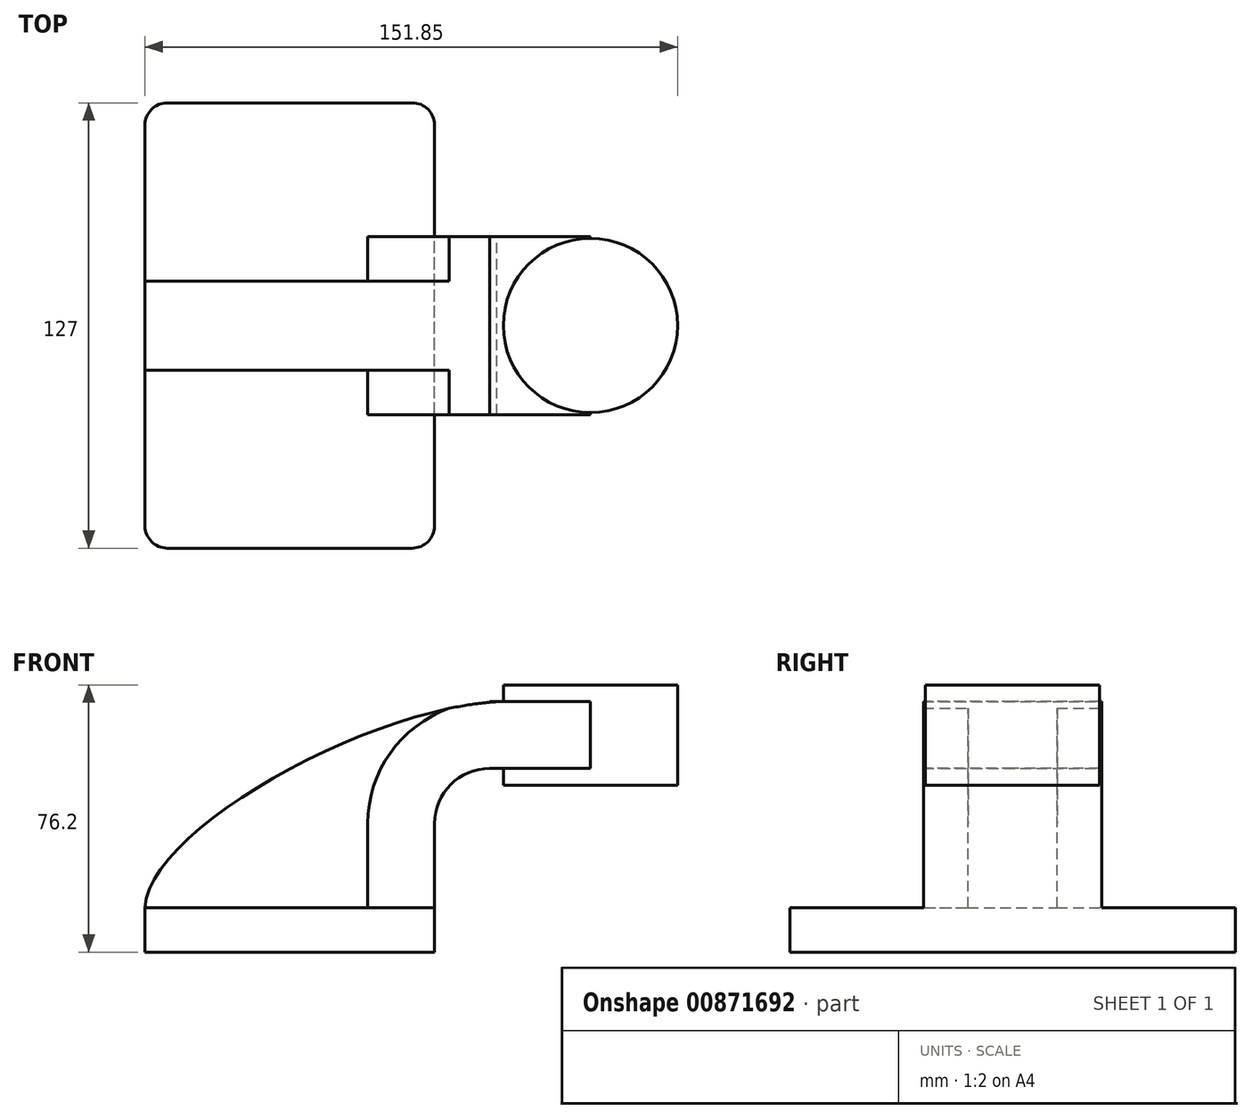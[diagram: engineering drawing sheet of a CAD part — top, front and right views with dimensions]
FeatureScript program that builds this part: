
annotation { "Feature Type Name" : "Feature", "Feature Type Description" : "" }
export const myFeature = defineFeature(function(context is Context, id is Id, definition is map)
    precondition{}
    {
        {
            var Q0;
            Q0=qCreatedBy(makeId("Front.planeOp"),FACE);
            var sketch = newSketch(context, id + "F0", { "sketchPlane" : qUnion([Q0])});
            skLineSegment(sketch, "E0.bottom", {"start": v(-41.28, 6.35) * mm, "end": v(41.28, 6.35) * mm});
            skLineSegment(sketch, "E0.top", {"start": v(-41.28, -6.35) * mm, "end": v(41.28, -6.35) * mm});
            skLineSegment(sketch, "E0.left", {"start": v(-41.28, 6.35) * mm, "end": v(-41.28, -6.35) * mm});
            skLineSegment(sketch, "E0.right", {"start": v(41.28, 6.35) * mm, "end": v(41.28, -6.35) * mm});
            skPoint(sketch, "E0.middle", {"position": v(0, 0) * mm});
            skLineSegment(sketch, "E1.bottom", {"start": v(59.77, 69.85) * mm, "end": v(110.57, 69.85) * mm});
            skLineSegment(sketch, "E1.top", {"start": v(59.77, 41.28) * mm, "end": v(110.57, 41.28) * mm});
            skLineSegment(sketch, "E1.left", {"start": v(59.77, 69.85) * mm, "end": v(59.77, 41.28) * mm});
            skLineSegment(sketch, "E1.right", {"start": v(110.57, 69.85) * mm, "end": v(110.57, 41.28) * mm});
            skLineSegment(sketch, "E2", {"start": v(41.28, 6.35) * mm, "end": v(41.28, 30.3) * mm});
            skArc(sketch, "E3", {"start": v(41.28, 30.3) * mm, "mid": v(45.89, 41.44) * mm, "end": v(57.02, 46.05) * mm});
            skLineSegment(sketch, "E4", {"start": v(57.02, 46.05) * mm, "end": v(85.72, 46.05) * mm});
            skLineSegment(sketch, "E5.0", {"start": v(22.23, 6.35) * mm, "end": v(22.23, 30.3) * mm});
            skArc(sketch, "E6.0", {"start": v(22.23, 30.3) * mm, "mid": v(33.13, 55.6) * mm, "end": v(59.02, 65.04) * mm});
            skLineSegment(sketch, "E7.0", {"start": v(57.02, 65.1) * mm, "end": v(85.72, 65.1) * mm});
            skLineSegment(sketch, "E8", {"start": v(85.72, 41.28) * mm, "end": v(85.72, 69.85) * mm});
            skPoint(sketch, "E8.startSnap0", {"position": v(85.17, 41.28) * mm});
            skFitSpline(sketch, "E9", {"points": [v(-41.28, 6.35) * mm, v(59.02, 65.04) * mm], "startDerivative": vector(2.25, 66.08) * mm, "endDerivative": vector(112.42, 6.48) * mm});
            skSolve(sketch);
        }
        {
            var Q0;
            Q0=makeQuery(id+"F0.imprint","IMPRINT",FACE,{"disambiguationData":[TD([[makeQuery(id+"F0.imprint","IMPRINT",EDGE,{"derivedFrom":sQuery(id+"F0.wireOp",EDGE,"E0.top")}),1.0]])]});
            extrude(context, id + "F1", {"entities" : qUnion([Q0]), "endBound" : BoundingType.SYMMETRIC, "depth" : 127 * mm, "offsetDistance" : 25.4 * mm});
        }
        {
            var Q0;
            {var subQ1=sQuery(id+"F0.wireOp",EDGE,"E2");Q0=makeQuery(id+"F0.imprint","IMPRINT",FACE,{"disambiguationData":[TD([[makeQuery(id+"F0.imprint","IMPRINT",EDGE,{"derivedFrom":subQ1}),1.0]])]});}
            var Q1;
            {var subQ0=sQuery(id+"F0.wireOp",EDGE,"E7.0");var subQ1=sQuery(id+"F0.wireOp",EDGE,"E1.left");var subQ2=makeQuery(id+"F0.imprint","INTERSECT",VERTEX,{"derivedFrom":[subQ1,subQ0]});Q1=makeQuery(id+"F0.imprint","IMPRINT",FACE,{"disambiguationData":[TD([[makeQuery(id+"F0.imprint","IMPRINT",EDGE,{"disambiguationData":[TD([[subQ2,-1.0]])],"derivedFrom":subQ1}),1.0]])]});}
            extrude(context, id + "F2", {"entities" : qUnion([Q0, Q1]), "operationType" : NewBodyOperationType.ADD, "endBound" : BoundingType.SYMMETRIC, "depth" : 50.8 * mm, "offsetDistance" : 25.4 * mm});
        }
        {
            var Q0;
            {var subQ3=sQuery(id+"F0.wireOp",EDGE,"E5.0");Q0=makeQuery(id+"F0.imprint","IMPRINT",FACE,{"disambiguationData":[TD([[makeQuery(id+"F0.imprint","IMPRINT",EDGE,{"derivedFrom":subQ3}),1.0]])]});}
            extrude(context, id + "F3", {"entities" : qUnion([Q0]), "operationType" : NewBodyOperationType.ADD, "endBound" : BoundingType.SYMMETRIC, "depth" : 25.4 * mm, "offsetDistance" : 25.4 * mm});
        }
        {
            var Q0;
            {var subQ0=sQuery(id+"F0.wireOp",EDGE,"E1.right");Q0=makeQuery(id+"F0.imprint","IMPRINT",FACE,{"disambiguationData":[TD([[makeQuery(id+"F0.imprint","IMPRINT",EDGE,{"derivedFrom":subQ0}),-1.0]])]});}
            var Q1;
            Q1=sQuery(id+"F0.wireOp",EDGE,"E8");
            revolve(context, id + "F4", {"operationType" : NewBodyOperationType.ADD, "surfaceOperationType" : NewSurfaceOperationType.NEW, "entities" : qUnion([Q0]), "axis" : qUnion([Q1]), "revolveType" : RevolveType.FULL});
        }
        {
            var Q0;
            Q0=makeQuery(id+"F1.opExtrude","CAP_EDGE",EDGE,{"disambiguationData":[OSD([sQuery(id+"F0.wireOp",EDGE,"E0.left")])],"isStart":false});
            var Q1;
            Q1=makeQuery(id+"F1.opExtrude","CAP_EDGE",EDGE,{"disambiguationData":[OSD([sQuery(id+"F0.wireOp",EDGE,"E0.right")])],"isStart":false});
            var Q2;
            Q2=makeQuery(id+"F1.opExtrude","CAP_EDGE",EDGE,{"disambiguationData":[OSD([sQuery(id+"F0.wireOp",EDGE,"E0.right")])],"isStart":true});
            var Q3;
            Q3=makeQuery(id+"F1.opExtrude","CAP_EDGE",EDGE,{"disambiguationData":[OSD([sQuery(id+"F0.wireOp",EDGE,"E0.left")])],"isStart":true});
            fillet(context, id + "F5", {"entities" : qUnion([Q0, Q1, Q2, Q3]), "radius" : 6.35 * mm, "tangentPropagation" : true, "allowEdgeOverflow" : false});
        }
    });
